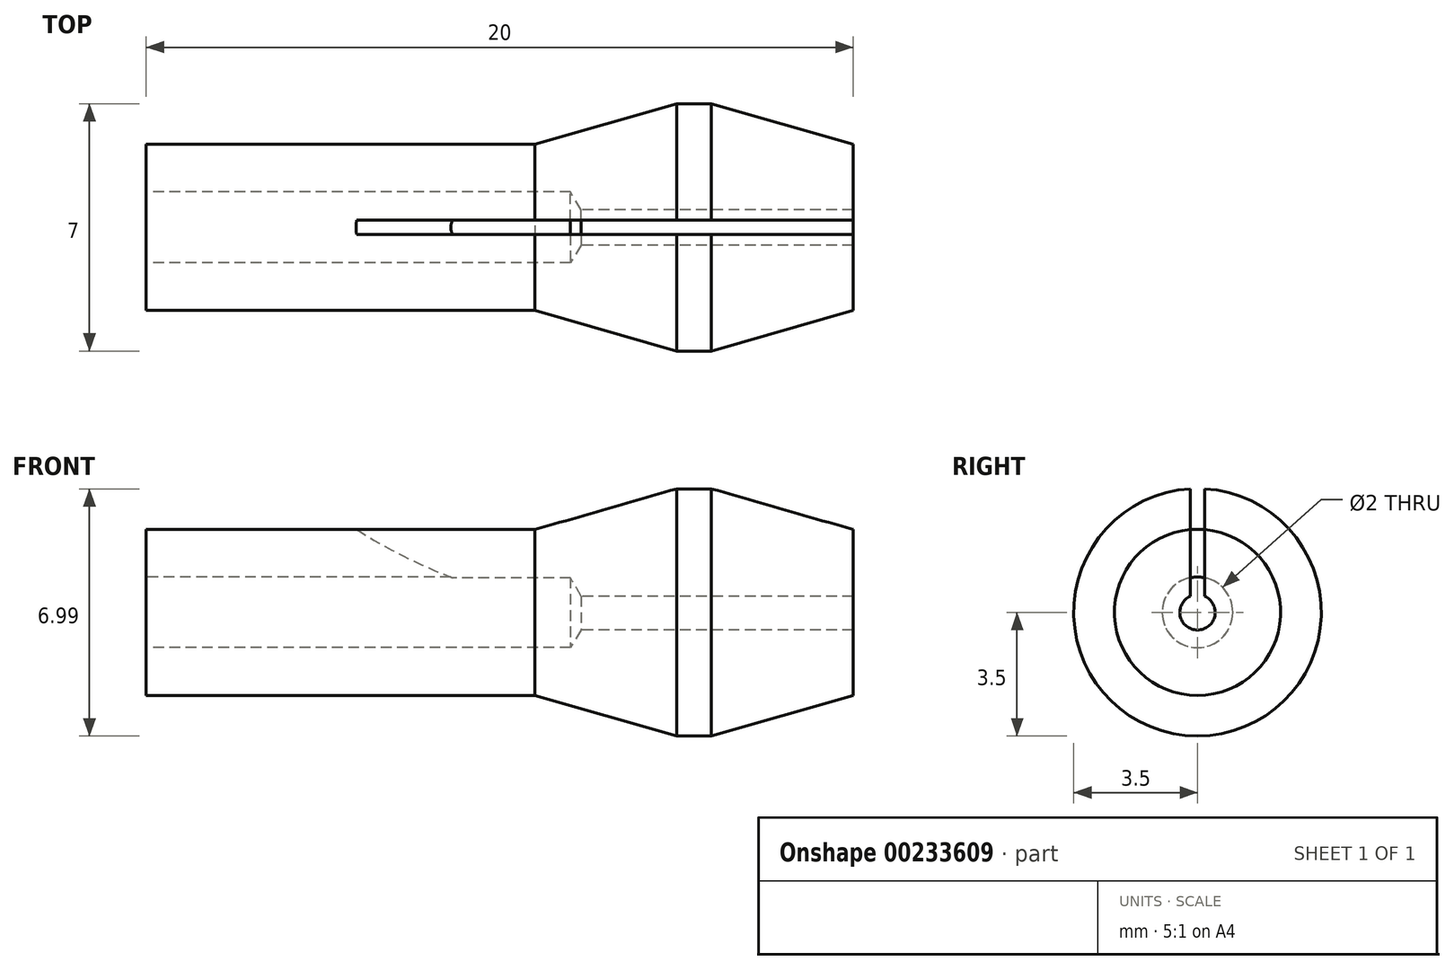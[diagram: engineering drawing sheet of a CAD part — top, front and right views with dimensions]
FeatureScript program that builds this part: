
annotation { "Feature Type Name" : "Feature", "Feature Type Description" : "" }
export const myFeature = defineFeature(function(context is Context, id is Id, definition is map)
    precondition{}
    {
        {
            var Q0;
            Q0=qCreatedBy(makeId("Front.planeOp"),FACE);
            var sketch = newSketch(context, id + "F0", { "sketchPlane" : qUnion([Q0])});
            skLineSegment(sketch, "E0", {"start": v(0, 1) * mm, "end": v(0, 2.35) * mm});
            skLineSegment(sketch, "E1", {"start": v(0, 2.35) * mm, "end": v(11, 2.35) * mm});
            skLineSegment(sketch, "E2", {"start": v(11, 2.35) * mm, "end": v(15.01, 3.5) * mm});
            skLineSegment(sketch, "E3", {"start": v(15.01, 3.5) * mm, "end": v(15.99, 3.5) * mm});
            skLineSegment(sketch, "E4", {"start": v(15.99, 3.5) * mm, "end": v(20, 2.35) * mm});
            skLineSegment(sketch, "E5", {"start": v(20, 2.35) * mm, "end": v(20, 0.5) * mm});
            skLineSegment(sketch, "E6", {"start": v(20, 0.5) * mm, "end": v(12.3, 0.5) * mm});
            skLineSegment(sketch, "E7", {"start": v(12.3, 0.5) * mm, "end": v(12, 1) * mm});
            skLineSegment(sketch, "E8", {"start": v(12, 1) * mm, "end": v(0, 1) * mm});
            skLineSegment(sketch, "E9", {"start": v(0, 0) * mm, "end": v(32.12, 0) * mm, "construction": true});
            skSolve(sketch);
        }
        {
            var Q0;
            Q0 = qSketchRegion(id + "F0", true);
            var Q1;
            Q1=sQuery(id+"F0.wireOp",EDGE,"E9");
            revolve(context, id + "F1", {"entities" : qUnion([Q0]), "axis" : qUnion([Q1]), "revolveType" : RevolveType.FULL});
        }
        {
            var Q0;
            Q0=qCreatedBy(makeId("Front.planeOp"),FACE);
            var sketch = newSketch(context, id + "F2", { "sketchPlane" : qUnion([Q0])});
            skLineSegment(sketch, "E10", {"start": v(0, 2.35) * mm, "end": v(11, 2.35) * mm});
            skLineSegment(sketch, "E11", {"start": v(0, 1) * mm, "end": v(12.4, 1) * mm});
            skLineSegment(sketch, "E12", {"start": v(12.4, -1) * mm, "end": v(0, -1) * mm});
            skLineSegment(sketch, "E13", {"start": v(12.7, 0.5) * mm, "end": v(20, 0.5) * mm});
            skLineSegment(sketch, "E14", {"start": v(20, -0.5) * mm, "end": v(12.7, -0.5) * mm});
            skLineSegment(sketch, "E15", {"start": v(12.1, 0.82) * mm, "end": v(12.4, 0.32) * mm});
            skLineSegment(sketch, "E16", {"start": v(12.4, -0.32) * mm, "end": v(12.1, -0.82) * mm});
            skCircle(sketch, "E17", {"center": v(14, 15) * mm, "radius": 15 * mm});
            skPoint(sketch, "E18", {"position": v(5.94, 2.35) * mm});
            skPoint(sketch, "E19", {"position": v(8.61, 1) * mm});
            skLineSegment(sketch, "E20.bottom", {"start": v(14, 15) * mm, "end": v(29, 15) * mm});
            skLineSegment(sketch, "E20.top", {"start": v(14, 0) * mm, "end": v(29, 0) * mm});
            skLineSegment(sketch, "E20.left", {"start": v(14, 15) * mm, "end": v(14, 0) * mm});
            skLineSegment(sketch, "E20.right", {"start": v(29, 15) * mm, "end": v(29, 0) * mm});
            skSolve(sketch);
        }
        {
            var Q0;
            Q0 = qSketchRegion(id + "F2", true);
            extrude(context, id + "F3", {"entities" : qUnion([Q0]), "operationType" : NewBodyOperationType.REMOVE, "endBound" : BoundingType.SYMMETRIC, "depth" : .4 * mm});
        }
    });
